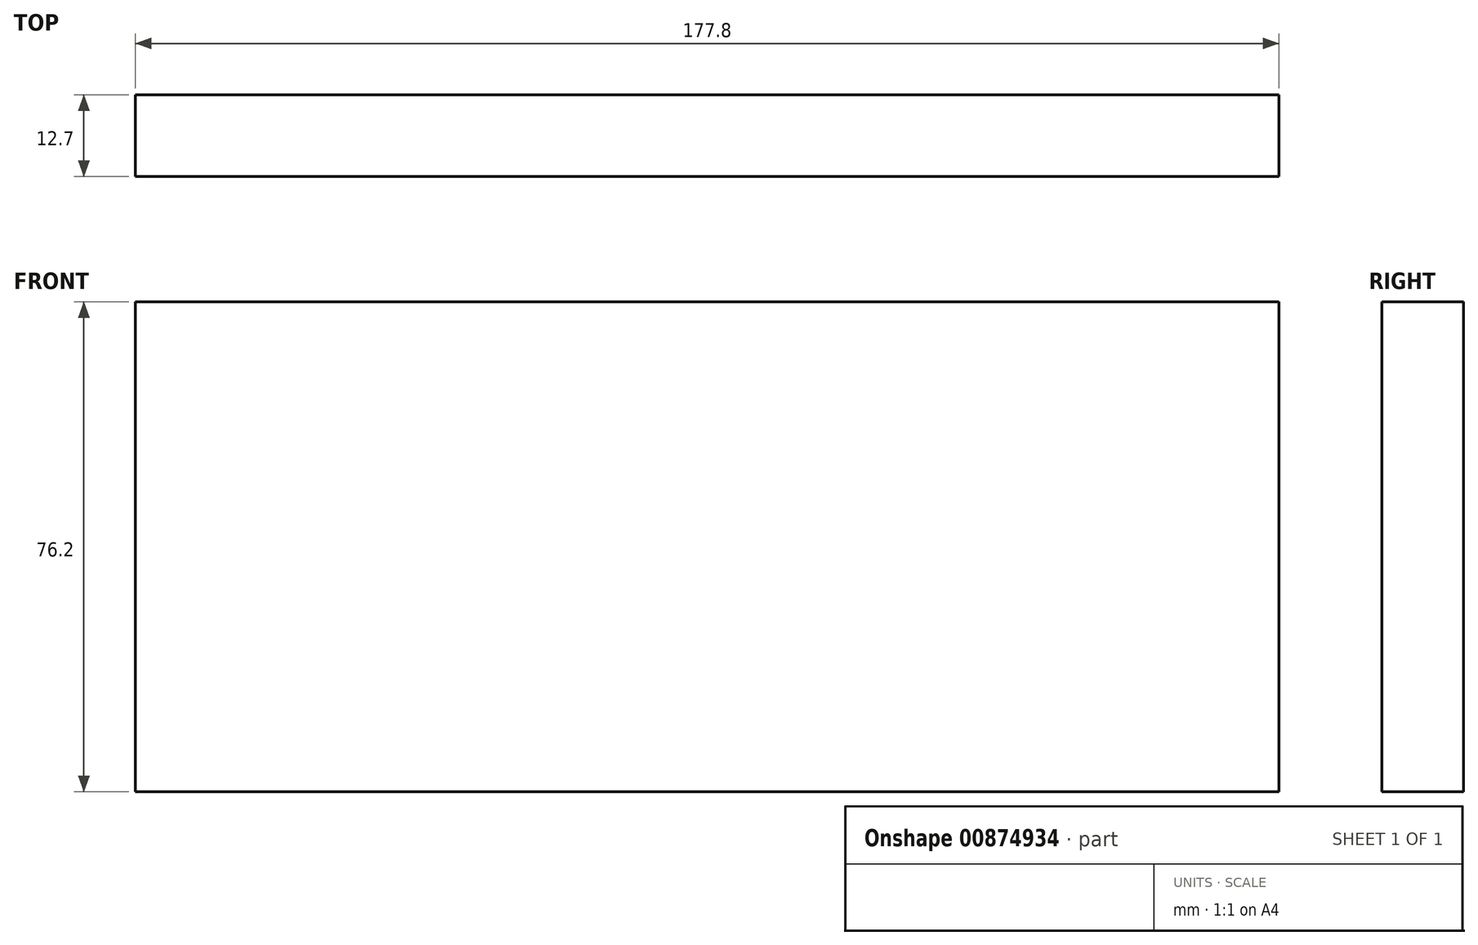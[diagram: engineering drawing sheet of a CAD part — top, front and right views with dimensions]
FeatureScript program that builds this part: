
annotation { "Feature Type Name" : "Feature", "Feature Type Description" : "" }
export const myFeature = defineFeature(function(context is Context, id is Id, definition is map)
    precondition{}
    {
        {
            var Q0;
            Q0=qCreatedBy(makeId("Front.planeOp"),FACE);
            var sketch = newSketch(context, id + "F0", { "sketchPlane" : qUnion([Q0])});
            skLineSegment(sketch, "E0.bottom", {"start": v(-88.9, 38.1) * mm, "end": v(88.9, 38.1) * mm});
            skLineSegment(sketch, "E0.top", {"start": v(-88.9, -38.1) * mm, "end": v(88.9, -38.1) * mm});
            skLineSegment(sketch, "E0.left", {"start": v(-88.9, 38.1) * mm, "end": v(-88.9, -38.1) * mm});
            skLineSegment(sketch, "E0.right", {"start": v(88.9, 38.1) * mm, "end": v(88.9, -38.1) * mm});
            skPoint(sketch, "E0.middle", {"position": v(0, 0) * mm});
            skSolve(sketch);
        }
        {
            var Q0;
            Q0=makeQuery(id+"F0.imprint","IMPRINT",FACE,{"disambiguationData":[TD([[makeQuery(id+"F0.imprint","IMPRINT",EDGE,{"derivedFrom":sQuery(id+"F0.wireOp",EDGE,"E0.bottom")}),-1.0]])]});
            extrude(context, id + "F1", {"entities" : qUnion([Q0]), "depth" : 12.7 * mm, "offsetDistance" : 25.4 * mm});
        }
    });
